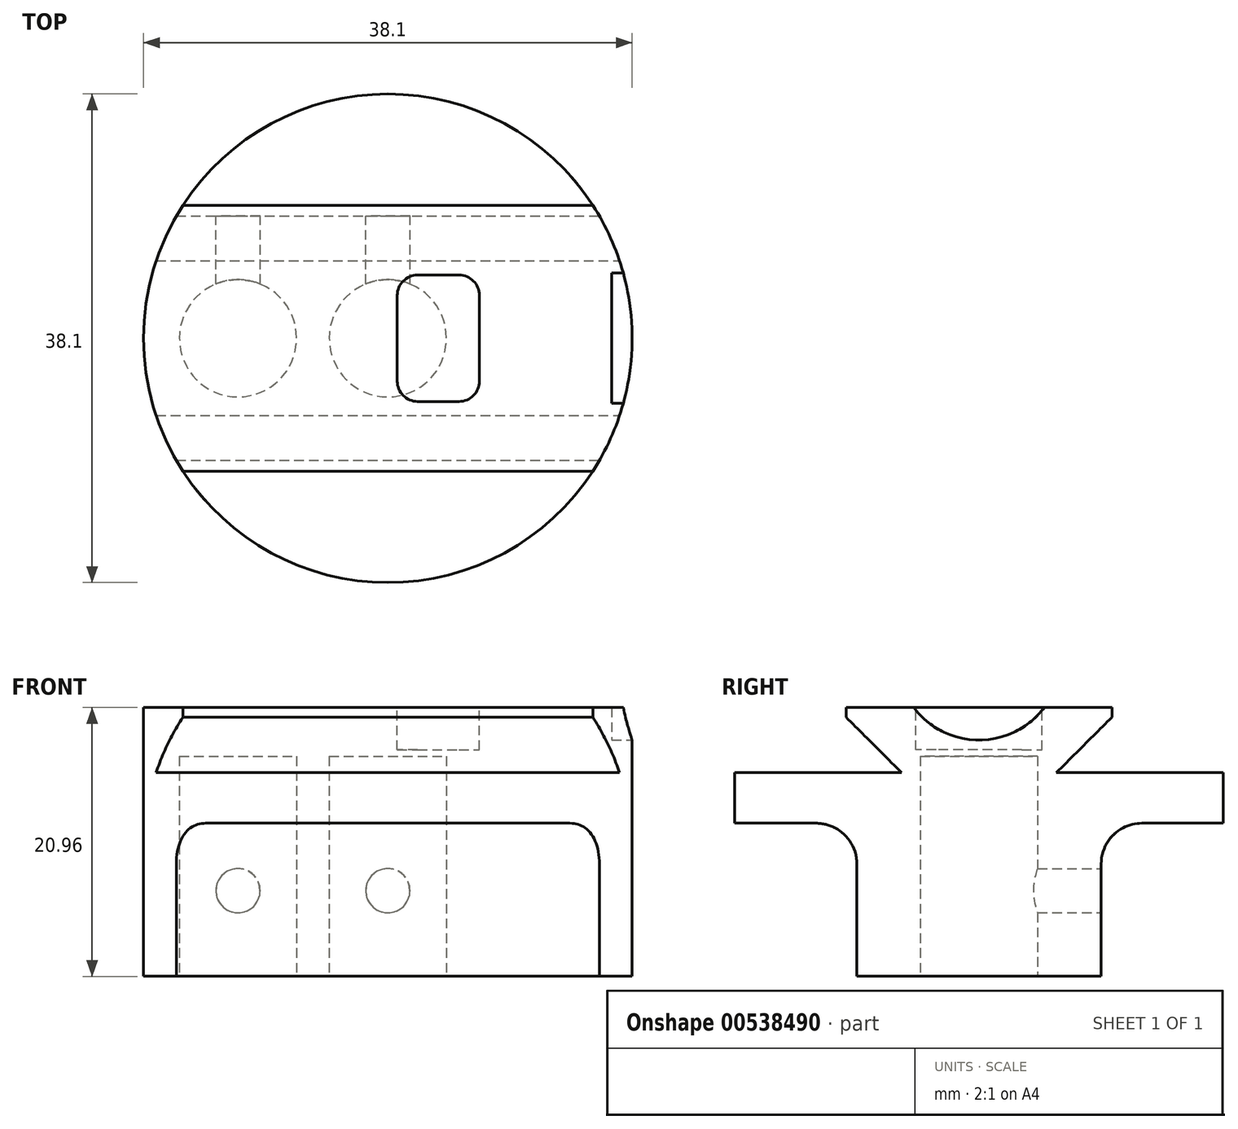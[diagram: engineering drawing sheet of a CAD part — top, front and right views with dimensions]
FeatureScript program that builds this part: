
annotation { "Feature Type Name" : "Feature", "Feature Type Description" : "" }
export const myFeature = defineFeature(function(context is Context, id is Id, definition is map)
    precondition{}
    {
        {
            var Q0;
            Q0=qCreatedBy(makeId("Top.planeOp"),FACE);
            var sketch = newSketch(context, id + "F0", { "sketchPlane" : qUnion([Q0])});
            skCircle(sketch, "E0", {"center": v(0, 0) * mm, "radius": 19.05 * mm});
            skSolve(sketch);
        }
        {
            var Q0;
            Q0=makeQuery(id+"F0.imprint","IMPRINT",FACE,{"disambiguationData":[TD([[makeQuery(id+"F0.imprint","IMPRINT",EDGE,{"derivedFrom":sQuery(id+"F0.wireOp",EDGE,"E0")}),1.0]])]});
            extrude(context, id + "F1", {"entities" : qUnion([Q0]), "oppositeDirection" : true, "depth" : 20.95 * mm, "offsetDistance" : 25.4 * mm});
        }
        {
            var Q0;
            Q0=qCreatedBy(makeId("Right.planeOp"),FACE);
            var sketch = newSketch(context, id + "F2", { "sketchPlane" : qUnion([Q0])});
            skLineSegment(sketch, "E1", {"start": v(-10.36, 0) * mm, "end": v(-10.36, -0.75) * mm});
            skLineSegment(sketch, "E2", {"start": v(-10.36, -0.75) * mm, "end": v(-6.03, -5.08) * mm});
            skLineSegment(sketch, "E3", {"start": v(-6.03, -5.08) * mm, "end": v(-19.05, -5.08) * mm});
            skLineSegment(sketch, "E4", {"start": v(-10.36, 0) * mm, "end": v(-19.05, 0) * mm});
            skLineSegment(sketch, "E5", {"start": v(-19.05, 0) * mm, "end": v(-19.05, -5.08) * mm});
            skLineSegment(sketch, "E6.MirrorCS", {"start": v(6.03, -5.08) * mm, "end": v(19.05, -5.08) * mm});
            skLineSegment(sketch, "E7.MirrorCS", {"start": v(10.36, -0.75) * mm, "end": v(6.03, -5.08) * mm});
            skLineSegment(sketch, "E8.MirrorCS", {"start": v(10.36, 0) * mm, "end": v(10.36, -0.75) * mm});
            skLineSegment(sketch, "E9.MirrorCS", {"start": v(10.36, 0) * mm, "end": v(19.05, 0) * mm});
            skLineSegment(sketch, "E10.MirrorCS", {"start": v(19.05, 0) * mm, "end": v(19.05, -5.08) * mm});
            skSolve(sketch);
        }
        {
            var Q0;
            Q0 = qSketchRegion(id + "F2", true);
            extrude(context, id + "F3", {"entities" : qUnion([Q0]), "operationType" : NewBodyOperationType.REMOVE, "endBound" : BoundingType.SYMMETRIC, "oppositeDirection" : true, "depth" : 50.8 * mm, "offsetDistance" : 25.4 * mm});
        }
        {
            var Q0;
            Q0=qCreatedBy(makeId("Right.planeOp"),FACE);
            var sketch = newSketch(context, id + "F4", { "sketchPlane" : qUnion([Q0])});
            skLineSegment(sketch, "E11", {"start": v(-9.52, -20.96) * mm, "end": v(-9.52, -12.2) * mm});
            skLineSegment(sketch, "E12", {"start": v(-12.7, -9.02) * mm, "end": v(-19.05, -9.02) * mm});
            skPoint(sketch, "E13.visualSharp", {"position": v(-9.52, -9.02) * mm});
            skArc(sketch, "E13.filletArc", {"start": v(-9.52, -12.2) * mm, "mid": v(-10.45, -9.95) * mm, "end": v(-12.7, -9.02) * mm});
            skLineSegment(sketch, "E14.MirrorCS", {"start": v(12.7, -9.02) * mm, "end": v(19.05, -9.02) * mm});
            skArc(sketch, "E15.MirrorCS", {"start": v(9.52, -12.2) * mm, "mid": v(10.45, -9.95) * mm, "end": v(12.7, -9.02) * mm});
            skLineSegment(sketch, "E16.MirrorCS", {"start": v(9.52, -20.96) * mm, "end": v(9.52, -12.2) * mm});
            skLineSegment(sketch, "E17", {"start": v(-19.05, -9.02) * mm, "end": v(-19.05, -20.96) * mm});
            skLineSegment(sketch, "E18", {"start": v(-19.05, -20.96) * mm, "end": v(-9.52, -20.96) * mm});
            skLineSegment(sketch, "E19.MirrorCS", {"start": v(19.05, -9.02) * mm, "end": v(19.05, -20.96) * mm});
            skLineSegment(sketch, "E20.MirrorCS", {"start": v(19.05, -20.96) * mm, "end": v(9.52, -20.96) * mm});
            skSolve(sketch);
        }
        {
            var Q0;
            Q0 = qSketchRegion(id + "F4", true);
            extrude(context, id + "F5", {"entities" : qUnion([Q0]), "operationType" : NewBodyOperationType.REMOVE, "endBound" : BoundingType.SYMMETRIC, "oppositeDirection" : true, "depth" : 50.8 * mm, "offsetDistance" : 25.4 * mm});
        }
        {
            var Q0;
            Q0=makeQuery(id+"F1.opExtrude","CAP_FACE",FACE,{"disambiguationData":[OSD([sQuery(id+"F0.wireOp",EDGE,"E0")])],"isStart":false});
            var sketch = newSketch(context, id + "F6", { "sketchPlane" : qUnion([Q0])});
            skCircle(sketch, "E21", {"center": v(0, 0) * mm, "radius": 4.57 * mm});
            skCircle(sketch, "E22", {"center": v(-11.68, 0) * mm, "radius": 4.57 * mm});
            skSolve(sketch);
        }
        {
            var Q0;
            Q0 = qSketchRegion(id + "F6", true);
            extrude(context, id + "F7", {"entities" : qUnion([Q0]), "operationType" : NewBodyOperationType.REMOVE, "oppositeDirection" : true, "depth" : 17.14 * mm, "offsetDistance" : 25.4 * mm});
        }
        {
            var Q0;
            Q0=makeQuery(id+"F5.boolean.opBoolean","COPY",FACE,{"derivedFrom":makeQuery(id+"F5.opExtrude","SWEPT_FACE",FACE,{"disambiguationData":[OSD([sQuery(id+"F4.wireOp",EDGE,"E16.MirrorCS")])]})});
            var sketch = newSketch(context, id + "F8", { "sketchPlane" : qUnion([Q0])});
            skPoint(sketch, "E23", {"position": v(0, -14.27) * mm});
            skPoint(sketch, "E23.positionSnap0", {"position": v(0, -20.96) * mm});
            skPoint(sketch, "E24", {"position": v(11.68, -14.27) * mm});
            skSolve(sketch);
        }
        {
            var Q0;
            Q0=sQuery(id+"F8.wireOp",VERTEX,"affa45d8-ab30-4e14-89b9-6c5f00e13c44");
            var Q1;
            Q1=sQuery(id+"F8.wireOp",VERTEX,"E23");
            var Q2;
            Q2=sQuery(id+"F8.wireOp",VERTEX,"E24");
            var Q3;
            Q3=makeQuery(id+"F1.opExtrude","SWEPT_BODY",BODY,{"disambiguationData":[OSD([sQuery(id+"F0.wireOp",EDGE,"E0")])]});
            hole(context, id + "F9", {"style" : HoleStyle.SIMPLE, "endStyle" : HoleEndStyle.BLIND, "standardTappedOrClearance" : lookupTablePath({ "standard" : "ANSI", "engagement" : "75%", "pitch" : "32 tpi", "size" : "#8", "type" : "Tapped" }), "standardBlindInLast" : lookupTablePath({ "standard" : "ANSI", "engagement" : "75%", "pitch" : "32 tpi", "size" : "#8", "type" : "Tapped" }), "holeDiameter" : 3.45 * mm, "showTappedDepth" : true, "holeDepth" : 10.8 * mm, "isTappedThrough" : true, "tappedDepth" : 8.43 * mm, "tapClearance" : 3, "startFromSketch" : true, "locations" : qUnion([Q0, Q1, Q2]), "scope" : qUnion([Q3]), "majorDiameter" : 4.17 * mm});
        }
        {
            var Q0;
            Q0=qCreatedBy(makeId("Right.planeOp"),FACE);
            cPlane(context, id + "F10", {"entities" : qUnion([Q0]), "cplaneType" : CPlaneType.OFFSET, "offset" : 19.05 * mm, "width" : 152.4 * mm, "height" : 152.4 * mm});
        }
        {
            var Q0;
            Q0=qCreatedBy(id+"F10.planeOp",FACE);
            var sketch = newSketch(context, id + "F11", { "sketchPlane" : qUnion([Q0])});
            skCircle(sketch, "E25", {"center": v(0, 3.81) * mm, "radius": 6.35 * mm});
            skSolve(sketch);
        }
        {
            var Q0;
            Q0=makeQuery(id+"F11.imprint","IMPRINT",FACE,{"disambiguationData":[TD([[makeQuery(id+"F11.imprint","IMPRINT",EDGE,{"derivedFrom":sQuery(id+"F11.wireOp",EDGE,"E25")}),1.0]])]});
            extrude(context, id + "F12", {"entities" : qUnion([Q0]), "operationType" : NewBodyOperationType.REMOVE, "oppositeDirection" : true, "depth" : 1.59 * mm, "offsetDistance" : 25.4 * mm});
        }
        {
            var Q0;
            Q0=makeQuery(id+"F1.opExtrude","CAP_FACE",FACE,{"disambiguationData":[OSD([sQuery(id+"F0.wireOp",EDGE,"E0")])],"isStart":true});
            var sketch = newSketch(context, id + "F13", { "sketchPlane" : qUnion([Q0])});
            skLineSegment(sketch, "E26.bottom", {"start": v(2.32, 4.93) * mm, "end": v(5.55, 4.93) * mm});
            skLineSegment(sketch, "E26.top", {"start": v(2.32, -4.93) * mm, "end": v(5.55, -4.93) * mm});
            skLineSegment(sketch, "E26.left", {"start": v(0.74, 3.34) * mm, "end": v(0.74, -3.34) * mm});
            skLineSegment(sketch, "E26.right", {"start": v(7.14, 3.34) * mm, "end": v(7.14, -3.34) * mm});
            skPoint(sketch, "E27.visualSharp", {"position": v(0.74, 4.93) * mm});
            skArc(sketch, "E27.filletArc", {"start": v(2.32, 4.93) * mm, "mid": v(1.2, 4.46) * mm, "end": v(0.74, 3.34) * mm});
            skPoint(sketch, "E28.visualSharp", {"position": v(0.74, -4.93) * mm});
            skArc(sketch, "E28.filletArc", {"start": v(0.74, -3.34) * mm, "mid": v(1.2, -4.46) * mm, "end": v(2.32, -4.93) * mm});
            skPoint(sketch, "E29.visualSharp", {"position": v(7.14, -4.93) * mm});
            skArc(sketch, "E29.filletArc", {"start": v(5.55, -4.93) * mm, "mid": v(6.67, -4.46) * mm, "end": v(7.14, -3.34) * mm});
            skPoint(sketch, "E30.visualSharp", {"position": v(7.14, 4.93) * mm});
            skArc(sketch, "E30.filletArc", {"start": v(7.14, 3.34) * mm, "mid": v(6.67, 4.46) * mm, "end": v(5.55, 4.93) * mm});
            skSolve(sketch);
        }
        {
            var Q0;
            Q0 = qSketchRegion(id + "F13", true);
            extrude(context, id + "F14", {"entities" : qUnion([Q0]), "operationType" : NewBodyOperationType.REMOVE, "oppositeDirection" : true, "depth" : 3.3 * mm, "offsetDistance" : 25.4 * mm});
        }
    });
